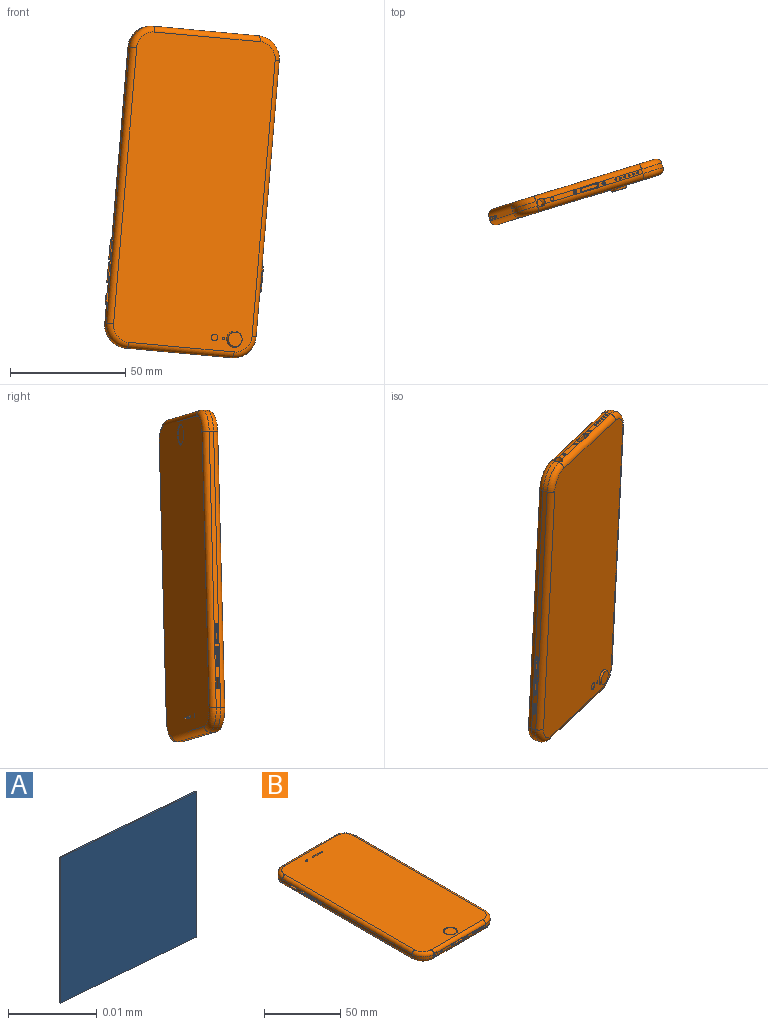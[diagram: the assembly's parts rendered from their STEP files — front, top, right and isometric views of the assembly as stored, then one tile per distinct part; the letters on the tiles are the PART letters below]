
ASSEMBLY  parts=2 mates=1
PART A: 6 faces, bbox 0x0x0 mm
  f0: plane 0.02x0mm, normal (-1,0.09,0), area 0mm2, adj f1,f3,f4,f5
  f1: plane 0.02x0mm, normal (0,0,1), area 0mm2, adj f0,f2,f4,f5
  f2: plane 0.02x0mm, normal (1,-0.09,0), area 0mm2, adj f1,f3,f4,f5
  f3: plane 0.02x0mm, normal (0,0,-1), area 0mm2, adj f0,f2,f4,f5
  f4: plane 0.02x0.02mm, normal (0.09,1,0), area 0mm2, adj f0,f1,f2,f3
  f5: plane 0.02x0.02mm, normal (-0.09,-1,0), area 0mm2, adj f0,f1,f2,f3
PART B: 155 faces, bbox 70x141.7x8 mm
  f0: plane 2x0.57mm, normal (0,-1,0), area 0.7mm2, adj f3,f6,f12,f19,f153,f154
  f1: cylinder r=2.5mm len=120mm, axis (0,-1,0), area 471.2mm2, adj f2,f16,f90,f96
  f2: torus R=7.5mm, axis (0,0,1), area 56.1mm2, adj f1,f3,f19,f90
  f3: cylinder r=2.5mm len=48mm, axis (1,0,0), area 186.2mm2, adj f0,f2,f5,f6,f9,f15,f28,f30
  f4: cylinder r=2.5mm len=120mm, axis (0,1,0), area 471.2mm2, adj f5,f17,f90,f94
  f5: torus R=7.5mm, axis (0,0,1), area 56.1mm2, adj f3,f4,f18,f90
  f6: cylinder r=1.75mm len=15mm, axis (0,-1,0), area 157.2mm2, adj f0,f3,f9,f12,f45,f81,f82,f83
  f7: plane 1.5x1.5mm, normal (0,-1,0), area 1.2mm2, adj f46,f61,f62,f63,f64,f65,f66,f67
  f8: plane 1.5x1.5mm, normal (0,-1,0), area 1.2mm2, adj f47,f50,f51,f52,f53,f54,f55,f56
  f9: plane 17x2mm, normal (0,-1,0), area 29.4mm2, adj f3,f6,f12,f26,f47,f48
  f10: cylinder r=2.5mm len=120mm, axis (0,1,0), area 471.2mm2, adj f11,f16,f75,f97
  f11: torus R=7.5mm, axis (0,0,1), area 56.1mm2, adj f10,f12,f19,f75
  f12: cylinder r=2.5mm len=48mm, axis (-1,0,0), area 185.8mm2, adj f0,f6,f9,f11,f14,f15,f25,f27
  f13: cylinder r=2.5mm len=120mm, axis (0,-1,0), area 471.2mm2, adj f14,f17,f75,f99
  f14: torus R=7.5mm, axis (0,0,1), area 56.1mm2, adj f12,f13,f18,f75
  f15: plane 20.43x2mm, normal (0,-1,0), area 34.8mm2, adj f3,f12,f18,f31,f33,f35,f37,f39
  f16: plane 120x2mm, normal (-1,0,0), area 216mm2, adj f1,f10,f19,f91,f125,f126,f127,f128
  f17: plane 120x2mm, normal (1,0,0), area 226.9mm2, adj f4,f13,f18,f93,f144,f145,f146,f147
  f18: cylinder r=10mm len=10mm, axis (0,0,-1), area 31.4mm2, adj f5,f14,f15,f17
  f19: cylinder r=10mm len=10mm, axis (0,0,-1), area 31.4mm2, adj f0,f2,f11,f16,f152
  f20: cylinder r=0.75mm len=2.6mm, axis (0,-1,0), area 6.1mm2, adj f21,f23,f24,f25,f26,f28
  f21: plane 6x2.59mm, normal (0,0,-1), area 15.6mm2, adj f20,f22,f24,f27
  f22: cylinder r=0.75mm len=2.6mm, axis (0,-1,0), area 6.1mm2, adj f21,f23,f24,f29,f31,f32
  f23: plane 6x2.59mm, normal (0,0,1), area 15.6mm2, adj f20,f22,f24,f30
  f24: plane 7.5x1.5mm, normal (0,-1,0), area 10.8mm2, adj f20,f21,f22,f23
  f25: bspline ~0.83x0.63mm, area 0.3mm2, adj f12,f20,f26,f27
  f26: torus R=1.15mm, axis (0,1,0), area 1.2mm2, adj f9,f20,f25,f28
  f27: cylinder r=0.4mm len=6mm, axis (-1,0,0), area 3.9mm2, adj f12,f21,f25,f29
  f28: bspline ~0.88x0.55mm, area 0.3mm2, adj f3,f20,f26,f30
  f29: bspline ~0.88x0.55mm, area 0.3mm2, adj f12,f22,f27,f31
  f30: cylinder r=0.4mm len=6mm, axis (1,0,0), area 3.9mm2, adj f3,f23,f28,f32
  f31: torus R=1.15mm, axis (0,1,0), area 1.2mm2, adj f15,f22,f29,f32
  f32: bspline ~0.83x0.63mm, area 0.3mm2, adj f3,f22,f30,f31
  f33: cylinder r=0.43mm len=1mm, axis (0,-1,0), area 2.7mm2, adj f15,f34
  f34: plane 0.86x0.86mm, normal (0,-1,0), area 0.6mm2, adj f33
  f35: cylinder r=0.43mm len=1mm, axis (0,-1,0), area 2.7mm2, adj f15,f36
  f36: plane 0.86x0.86mm, normal (0,-1,0), area 0.6mm2, adj f35
  f37: cylinder r=0.43mm len=1mm, axis (0,-1,0), area 2.7mm2, adj f15,f38
  f38: plane 0.86x0.86mm, normal (0,-1,0), area 0.6mm2, adj f37
  f39: cylinder r=0.43mm len=1mm, axis (0,-1,0), area 2.7mm2, adj f15,f40
  f40: plane 0.86x0.86mm, normal (0,-1,0), area 0.6mm2, adj f39
  f41: cylinder r=0.43mm len=1mm, axis (0,-1,0), area 2.7mm2, adj f15,f42
  f42: plane 0.86x0.86mm, normal (0,-1,0), area 0.6mm2, adj f41
  f43: cylinder r=0.43mm len=1mm, axis (0,-1,0), area 2.7mm2, adj f15,f44
  f44: plane 0.86x0.86mm, normal (0,-1,0), area 0.6mm2, adj f43
  f45: plane 3.5x3.5mm, normal (0,-1,0), area 9.6mm2, adj f6
  f46: cylinder r=0.75mm len=1.5mm, axis (0,-1,0), area 1.2mm2, adj f7,f15
  f47: cylinder r=0.75mm len=1.5mm, axis (0,-1,0), area 1.2mm2, adj f8,f9
  f48: cylinder r=0.7mm len=1.4mm, axis (0,-1,0), area 1.1mm2, adj f9,f49
  f49: plane 1.4x1.4mm, normal (0,-1,0), area 1.5mm2, adj f48
  f50: extruded ~0.5x0.29mm, area 0.3mm2, adj f8,f51,f59,f60
  f51: extruded ~0.5x0.16mm, area 0.1mm2, adj f8,f50,f52,f60
  f52: extruded ~0.5x0.26mm, area 0.3mm2, adj f8,f51,f53,f60
  f53: extruded ~0.5x0.16mm, area 0.1mm2, adj f8,f52,f54,f60
  f54: extruded ~0.5x0.26mm, area 0.3mm2, adj f8,f53,f55,f60
  f55: extruded ~0.5x0.15mm, area 0.1mm2, adj f8,f54,f56,f60
  f56: extruded ~0.5x0.28mm, area 0.3mm2, adj f8,f55,f57,f60
  f57: extruded ~0.5x0.13mm, area 0.1mm2, adj f8,f56,f58,f60
  f58: extruded ~0.5x0.3mm, area 0.3mm2, adj f8,f57,f59,f60
  f59: extruded ~0.5x0.13mm, area 0.1mm2, adj f8,f50,f58,f60
  f60: plane 1.18x1.14mm, normal (0,-1,0), area 0.6mm2, adj f50,f51,f52,f53,f54,f55,f56,f57
  f61: extruded ~0.5x0.3mm, area 0.3mm2, adj f7,f62,f70,f71
  f62: extruded ~0.5x0.13mm, area 0.1mm2, adj f7,f61,f63,f71
  f63: extruded ~0.5x0.29mm, area 0.3mm2, adj f7,f62,f64,f71
  f64: extruded ~0.5x0.16mm, area 0.1mm2, adj f7,f63,f65,f71
  f65: extruded ~0.5x0.26mm, area 0.3mm2, adj f7,f64,f66,f71
  f66: extruded ~0.5x0.16mm, area 0.1mm2, adj f7,f65,f67,f71
  f67: extruded ~0.5x0.26mm, area 0.3mm2, adj f7,f66,f68,f71
  f68: extruded ~0.5x0.15mm, area 0.1mm2, adj f7,f67,f69,f71
  f69: extruded ~0.5x0.28mm, area 0.3mm2, adj f7,f68,f70,f71
  f70: extruded ~0.5x0.13mm, area 0.1mm2, adj f7,f61,f69,f71
  f71: plane 1.18x1.14mm, normal (0,-1,0), area 0.6mm2, adj f61,f62,f63,f64,f65,f66,f67,f68
  f72: cone r=4.06mm half-angle=64.1deg, axis (0,0,1), area 13.1mm2, adj f73,f75
  f73: plane 8.13x8.13mm, normal (0,0,1), area 51.9mm2, adj f72
  f74: cylinder r=0.75mm len=1.5mm, axis (0,0,1), area 4.7mm2, adj f75,f148
  f75: plane 135.02x63.02mm, normal (0,0,1), area 8382.3mm2, adj f10,f11,f12,f13,f14,f72,f74,f77
  f76: plane 9x1mm, normal (0,0,1), area 8.8mm2, adj f77,f78,f79,f80
  f77: cylinder r=0.5mm len=1.99mm, axis (0,0,1), area 3.1mm2, adj f75,f76,f78,f79
  f78: plane 8x1.99mm, normal (0,1,0), area 15.9mm2, adj f75,f76,f77,f80
  f79: plane 8x1.99mm, normal (0,-1,0), area 15.9mm2, adj f75,f76,f77,f80
  f80: cylinder r=0.5mm len=1.99mm, axis (0,0,1), area 3.1mm2, adj f75,f76,f78,f79
  f81: plane 1.8x0.25mm, normal (0,1,0), area 0.3mm2, adj f6,f83
  f82: plane 1.8x0.25mm, normal (0,-1,0), area 0.3mm2, adj f6,f83
  f83: plane 2x1.8mm, normal (0,0,1), area 3.6mm2, adj f6,f81,f82
  f84: plane 1.8x0.25mm, normal (0,-1,0), area 0.3mm2, adj f6,f86
  f85: plane 1.8x0.25mm, normal (0,1,0), area 0.3mm2, adj f6,f86
  f86: plane 2x1.8mm, normal (0,0,1), area 3.6mm2, adj f6,f84,f85
  f87: cone r=3.5mm half-angle=20deg, axis (0,0,1), area 22.2mm2, adj f90,f150
  f88: cylinder r=0.5mm len=1mm, axis (0,0,-1), area 0.8mm2, adj f90,f149
  f89: cylinder r=1.5mm len=3mm, axis (0,0,-1), area 2.4mm2, adj f90,f151
  f90: plane 135x63mm, normal (0,0,-1), area 8410.4mm2, adj f1,f2,f3,f4,f5,f87,f88,f89
  f91: cylinder r=10mm len=10mm, axis (0,0,-1), area 31.4mm2, adj f16,f92,f96,f97
  f92: plane 48x2mm, normal (0,1,0), area 96mm2, adj f91,f93,f95,f98
  f93: cylinder r=10mm len=10mm, axis (0,0,-1), area 31.4mm2, adj f17,f92,f94,f99
  f94: torus R=7.5mm, axis (0,0,1), area 56.1mm2, adj f4,f90,f93,f95
  f95: cylinder r=2.5mm len=48mm, axis (-1,0,0), area 188.5mm2, adj f90,f92,f94,f96
  f96: torus R=7.5mm, axis (0,0,1), area 56.1mm2, adj f1,f90,f91,f95
  f97: torus R=7.5mm, axis (0,0,1), area 56.1mm2, adj f10,f75,f91,f98
  f98: cylinder r=2.5mm len=48mm, axis (1,0,0), area 188.5mm2, adj f75,f92,f97,f99
  f99: torus R=7.5mm, axis (0,0,1), area 56.1mm2, adj f13,f75,f93,f98
  f100: plane 4.6x0.25mm, normal (-1,0,0), area 1.2mm2, adj f106,f108,f110,f112
  f101: plane 8.2x0.2mm, normal (-1,0,0), area 1.6mm2, adj f113,f114,f115,f116
  f102: plane 8.2x0.2mm, normal (-1,0,0), area 1.6mm2, adj f117,f118,f119,f120
  f103: plane 10.4x0.4mm, normal (1,0,0), area 4.1mm2, adj f121,f122,f123,f124
  f104: sphere r=0.2mm, area 0.1mm2, adj f106,f112,f125
  f105: plane 5x0.65mm, normal (-1,0,0), area 3.2mm2, adj f126,f127,f128,f129
  f106: cylinder r=0.2mm len=4.6mm, axis (0,-1,0), area 1.4mm2, adj f100,f104,f107,f129
  f107: sphere r=0.2mm, area 0.1mm2, adj f106,f108,f130
  f108: cylinder r=0.2mm len=0.25mm, axis (0,0,1), area 0.1mm2, adj f100,f107,f109,f131
  f109: sphere r=0.2mm, area 0.1mm2, adj f108,f110,f132
  f110: cylinder r=0.2mm len=4.6mm, axis (0,1,0), area 1.4mm2, adj f100,f109,f111,f133
  f111: sphere r=0.2mm, area 0.1mm2, adj f110,f112,f134
  f112: cylinder r=0.2mm len=0.25mm, axis (0,0,-1), area 0.1mm2, adj f100,f104,f111,f135
  f113: cylinder r=0.4mm len=8mm, axis (0,1,0), area 5mm2, adj f101,f114,f116,f136
  f114: torus R=0.1mm, axis (-1,0,0), area 0.7mm2, adj f101,f113,f115,f137
  f115: cylinder r=0.4mm len=8mm, axis (0,-1,0), area 5mm2, adj f101,f114,f116,f138
  f116: torus R=0.1mm, axis (-1,0,0), area 0.7mm2, adj f101,f113,f115,f139
  f117: cylinder r=0.4mm len=8mm, axis (0,1,0), area 5mm2, adj f102,f118,f120,f140
  f118: torus R=0.1mm, axis (-1,0,0), area 0.7mm2, adj f102,f117,f119,f141
  f119: cylinder r=0.4mm len=8mm, axis (0,-1,0), area 5mm2, adj f102,f118,f120,f142
  f120: torus R=0.1mm, axis (-1,0,0), area 0.7mm2, adj f102,f117,f119,f143
  f121: cylinder r=0.4mm len=10mm, axis (0,1,0), area 6.3mm2, adj f103,f122,f124,f144
  f122: torus R=0.2mm, axis (1,0,0), area 0.9mm2, adj f103,f121,f123,f145
  f123: cylinder r=0.4mm len=10mm, axis (0,-1,0), area 6.3mm2, adj f103,f122,f124,f146
  f124: torus R=0.2mm, axis (1,0,0), area 0.9mm2, adj f103,f121,f123,f147
  f125: cylinder r=0.2mm len=0.8mm, axis (1,0,0), area 0.3mm2, adj f16,f104,f129,f135
  f126: plane 1x0.65mm, normal (0,1,0), area 0.7mm2, adj f16,f105,f127,f129
  f127: plane 5x1mm, normal (0,0,-1), area 5mm2, adj f16,f105,f126,f128
  f128: plane 1x0.65mm, normal (0,-1,0), area 0.7mm2, adj f16,f105,f127,f129
  f129: plane 5x1.8mm, normal (0,0,1), area 8.7mm2, adj f16,f105,f106,f125,f126,f128,f130
  f130: cylinder r=0.2mm len=0.8mm, axis (1,0,0), area 0.3mm2, adj f16,f107,f129,f131
  f131: plane 0.8x0.25mm, normal (0,1,0), area 0.2mm2, adj f16,f108,f130,f132
  f132: cylinder r=0.2mm len=0.8mm, axis (1,0,0), area 0.3mm2, adj f16,f109,f131,f133
  f133: plane 4.6x0.8mm, normal (0,0,-1), area 3.7mm2, adj f16,f110,f132,f134
  f134: cylinder r=0.2mm len=0.8mm, axis (1,0,0), area 0.3mm2, adj f16,f111,f133,f135
  f135: plane 0.8x0.25mm, normal (0,-1,0), area 0.2mm2, adj f16,f112,f125,f134
  f136: plane 8x0.6mm, normal (0,0,-1), area 4.8mm2, adj f16,f113,f137,f139
  f137: cylinder r=0.5mm len=1mm, axis (1,0,0), area 0.9mm2, adj f16,f114,f136,f138
  f138: plane 8x0.6mm, normal (0,0,1), area 4.8mm2, adj f16,f115,f137,f139
  f139: cylinder r=0.5mm len=1mm, axis (1,0,0), area 0.9mm2, adj f16,f116,f136,f138
  f140: plane 8x0.6mm, normal (0,0,-1), area 4.8mm2, adj f16,f117,f141,f143
  f141: cylinder r=0.5mm len=1mm, axis (1,0,0), area 0.9mm2, adj f16,f118,f140,f142
  f142: plane 8x0.6mm, normal (0,0,1), area 4.8mm2, adj f16,f119,f141,f143
  f143: cylinder r=0.5mm len=1mm, axis (1,0,0), area 0.9mm2, adj f16,f120,f140,f142
  f144: plane 10x0.6mm, normal (0,0,1), area 6mm2, adj f17,f121,f145,f147
  f145: cylinder r=0.6mm len=1.2mm, axis (-1,0,0), area 1.1mm2, adj f17,f122,f144,f146
  f146: plane 10x0.6mm, normal (0,0,-1), area 6mm2, adj f17,f123,f145,f147
  f147: cylinder r=0.6mm len=1.2mm, axis (-1,0,0), area 1.1mm2, adj f17,f124,f144,f146
  f148: plane 1.5x1.5mm, normal (0,0,1), area 1.8mm2, adj f74
  f149: plane 1x1mm, normal (0,0,-1), area 0.8mm2, adj f88
  f150: plane 6.27x6.27mm, normal (0,0,-1), area 30.9mm2, adj f87
  f151: plane 3x3mm, normal (0,0,-1), area 7.1mm2, adj f89
  f152: plane 0.02x0mm, normal (-1,0.09,0), area 0mm2, adj f19,f153,f154
  f153: plane 0.02x0mm, normal (0,0,-1), area 0mm2, adj f0,f152,f154
  f154: plane 0.02x0.02mm, normal (-0.09,-1,0), area 0mm2, adj f0,f12,f152,f153
PLACE A rot(axis=(1,-0.04,0.04),90.1deg) t=(9.3,-80.08,92.61)mm fixed
PLACE B rot(axis=(-0.98,-0.1,0.19),92.1deg) t=(9.83,-83.63,-76.04)mm
MATE revolute B.f154 <-> A.f4  axis (0,0,1) through (-8.5,-84.56,-4.22)mm
